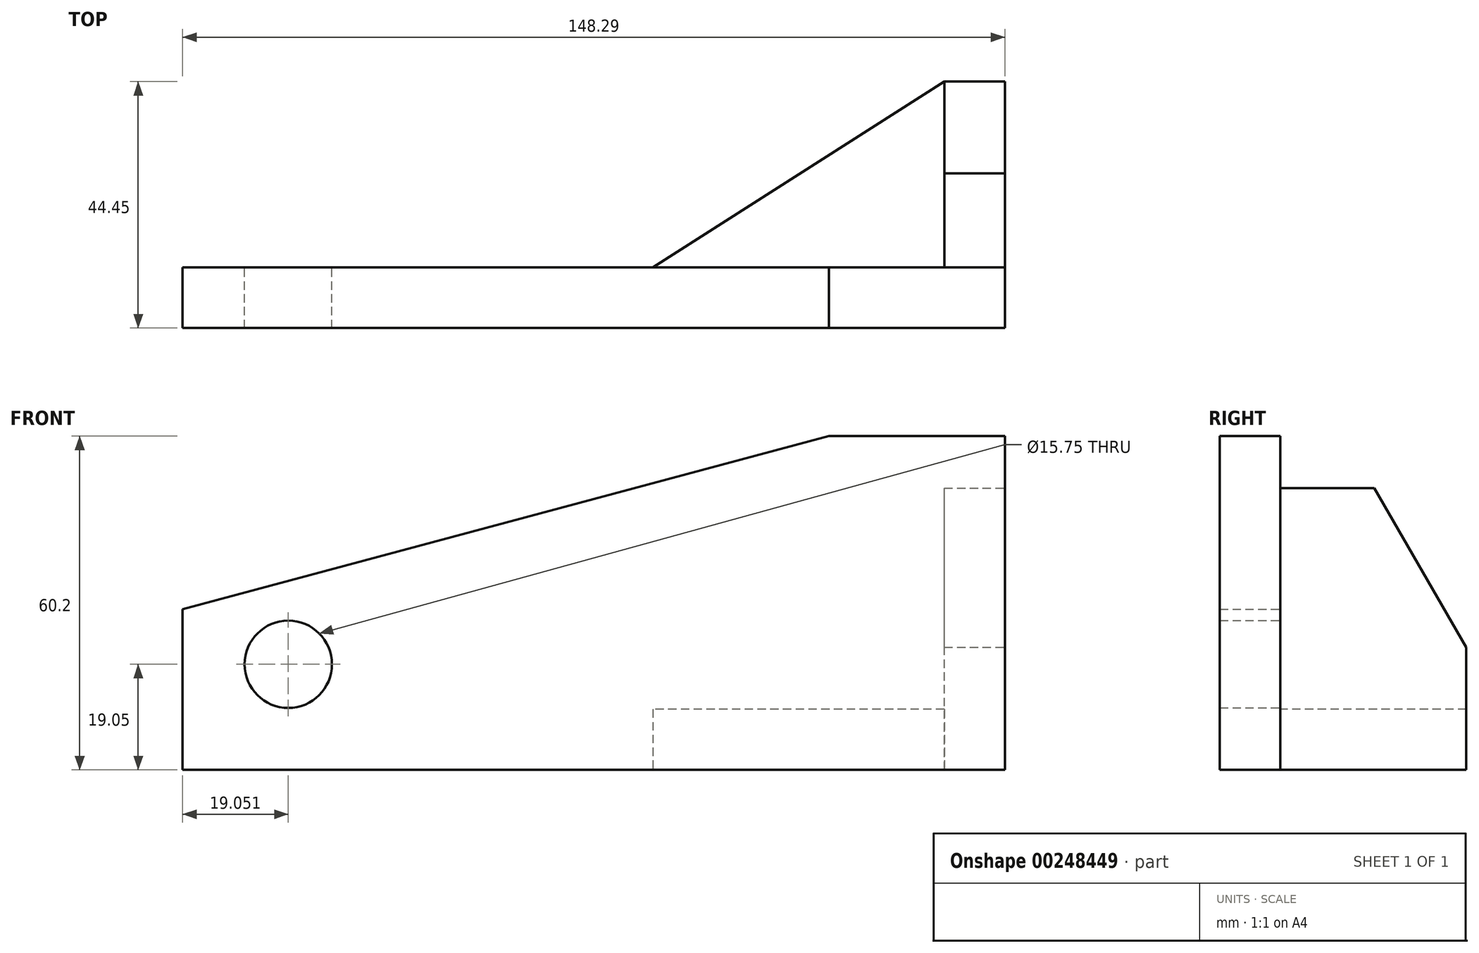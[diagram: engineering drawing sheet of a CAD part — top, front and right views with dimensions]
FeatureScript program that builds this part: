
annotation { "Feature Type Name" : "Feature", "Feature Type Description" : "" }
export const myFeature = defineFeature(function(context is Context, id is Id, definition is map)
    precondition{}
    {
        {
            var Q0;
            Q0=qCreatedBy(makeId("Front.planeOp"),FACE);
            var sketch = newSketch(context, id + "F0", { "sketchPlane" : qUnion([Q0])});
            skLineSegment(sketch, "E0.bottom", {"start": v(0, 0) * mm, "end": v(-148.29, 0) * mm});
            skLineSegment(sketch, "E0.top", {"start": v(0, 60.2) * mm, "end": v(-31.75, 60.2) * mm});
            skLineSegment(sketch, "E0.left", {"start": v(0, 0) * mm, "end": v(0, 60.2) * mm});
            skLineSegment(sketch, "E0.right", {"start": v(-148.29, 0) * mm, "end": v(-148.29, 28.97) * mm});
            skLineSegment(sketch, "E1", {"start": v(-31.75, 60.2) * mm, "end": v(-148.29, 28.97) * mm});
            skCircle(sketch, "E2", {"center": v(-129.24, 19.05) * mm, "radius": 7.87 * mm});
            skSolve(sketch);
        }
        {
            var Q0;
            {var subQ1=sQuery(id+"F0.wireOp",EDGE,"E0.bottom");Q0=makeQuery(id+"F0.imprint","IMPRINT",FACE,{"disambiguationData":[TD([[makeQuery(id+"F0.imprint","IMPRINT",EDGE,{"derivedFrom":subQ1}),-1.0]])]});}
            extrude(context, id + "F1", {"entities" : qUnion([Q0]), "depth" : 10.92 * mm});
        }
        {
            var Q0;
            Q0=qCreatedBy(makeId("Right.planeOp"),FACE);
            var sketch = newSketch(context, id + "F2", { "sketchPlane" : qUnion([Q0])});
            skLineSegment(sketch, "E3.bottom", {"start": v(0, 0) * mm, "end": v(33.53, 0) * mm});
            skLineSegment(sketch, "E3.top", {"start": v(0, 50.8) * mm, "end": v(33.53, 50.8) * mm});
            skLineSegment(sketch, "E3.left", {"start": v(0, 0) * mm, "end": v(0, 50.8) * mm});
            skLineSegment(sketch, "E3.right", {"start": v(33.53, 0) * mm, "end": v(33.53, 50.8) * mm});
            skLineSegment(sketch, "E4", {"start": v(33.53, 22.1) * mm, "end": v(16.96, 50.8) * mm});
            skSolve(sketch);
        }
        {
            var Q0;
            {var subQ1=sQuery(id+"F2.wireOp",EDGE,"E3.bottom");Q0=makeQuery(id+"F2.imprint","IMPRINT",FACE,{"disambiguationData":[TD([[makeQuery(id+"F2.imprint","IMPRINT",EDGE,{"derivedFrom":subQ1}),1.0]])]});}
            extrude(context, id + "F3", {"entities" : qUnion([Q0]), "oppositeDirection" : true, "depth" : 10.92 * mm});
        }
        {
            var Q0;
            Q0=qCreatedBy(makeId("Top.planeOp"),FACE);
            var sketch = newSketch(context, id + "F4", { "sketchPlane" : qUnion([Q0])});
            skLineSegment(sketch, "E5.bottom", {"start": v(0, 0) * mm, "end": v(-63.5, 0) * mm});
            skLineSegment(sketch, "E5.top", {"start": v(0, 33.53) * mm, "end": v(-63.5, 33.53) * mm});
            skLineSegment(sketch, "E5.left", {"start": v(0, 0) * mm, "end": v(0, 33.53) * mm});
            skLineSegment(sketch, "E5.right", {"start": v(-63.5, 0) * mm, "end": v(-63.5, 33.53) * mm});
            skLineSegment(sketch, "E6", {"start": v(-10.92, 33.53) * mm, "end": v(-10.92, 0) * mm});
            skLineSegment(sketch, "E7", {"start": v(-10.92, 33.53) * mm, "end": v(-63.5, 0) * mm});
            skSolve(sketch);
        }
        {
            var Q0;
            {var subQ2=sQuery(id+"F4.wireOp",EDGE,"E6");Q0=makeQuery(id+"F4.imprint","IMPRINT",FACE,{"disambiguationData":[TD([[makeQuery(id+"F4.imprint","IMPRINT",EDGE,{"derivedFrom":subQ2}),-1.0]])]});}
            extrude(context, id + "F5", {"entities" : qUnion([Q0]), "depth" : 10.92 * mm});
        }
    });
